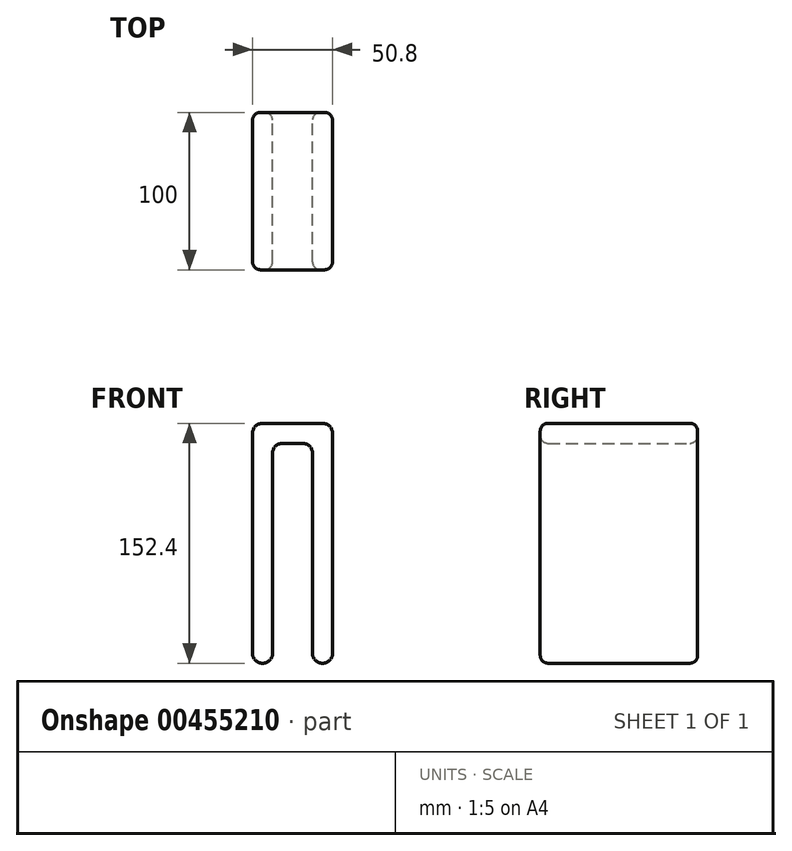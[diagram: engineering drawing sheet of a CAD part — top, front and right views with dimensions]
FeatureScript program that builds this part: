
annotation { "Feature Type Name" : "Feature", "Feature Type Description" : "" }
export const myFeature = defineFeature(function(context is Context, id is Id, definition is map)
    precondition{}
    {
        {
            var Q0;
            Q0=qCreatedBy(makeId("Front.planeOp"),FACE);
            var sketch = newSketch(context, id + "F0", { "sketchPlane" : qUnion([Q0])});
            skLineSegment(sketch, "E0.bottom", {"start": v(-19.05, 76.2) * mm, "end": v(19.05, 76.2) * mm});
            skLineSegment(sketch, "E0.top", {"start": v(-19.05, -76.2) * mm, "end": v(-19.05, -76.2) * mm});
            skLineSegment(sketch, "E0.left", {"start": v(-25.4, 69.85) * mm, "end": v(-25.4, -69.85) * mm});
            skLineSegment(sketch, "E0.right", {"start": v(25.4, 69.85) * mm, "end": v(25.4, -69.85) * mm});
            skPoint(sketch, "E0.middle", {"position": v(0, 0) * mm});
            skLineSegment(sketch, "E1.top", {"start": v(-6.35, 63.5) * mm, "end": v(6.35, 63.5) * mm});
            skLineSegment(sketch, "E1.left", {"start": v(-12.7, -63.5) * mm, "end": v(-12.7, 57.15) * mm});
            skLineSegment(sketch, "E1.right", {"start": v(12.7, -63.5) * mm, "end": v(12.7, 57.15) * mm});
            skLineSegment(sketch, "E2", {"start": v(-12.7, -63.5) * mm, "end": v(-12.7, -69.85) * mm});
            skLineSegment(sketch, "E3", {"start": v(12.7, -63.5) * mm, "end": v(12.7, -69.85) * mm});
            skLineSegment(sketch, "E4.trimOffspring", {"start": v(19.05, -76.2) * mm, "end": v(19.05, -76.2) * mm});
            skPoint(sketch, "E5.visualSharp", {"position": v(-12.7, 63.5) * mm});
            skArc(sketch, "E5.filletArc", {"start": v(-6.35, 63.5) * mm, "mid": v(-10.84, 61.64) * mm, "end": v(-12.7, 57.15) * mm});
            skPoint(sketch, "E6.visualSharp", {"position": v(-25.4, 76.2) * mm});
            skArc(sketch, "E6.filletArc", {"start": v(-19.05, 76.2) * mm, "mid": v(-23.54, 74.34) * mm, "end": v(-25.4, 69.85) * mm});
            skPoint(sketch, "E7.visualSharp", {"position": v(25.4, 76.2) * mm});
            skArc(sketch, "E7.filletArc", {"start": v(25.4, 69.85) * mm, "mid": v(23.54, 74.34) * mm, "end": v(19.05, 76.2) * mm});
            skPoint(sketch, "E8.visualSharp", {"position": v(12.7, 63.5) * mm});
            skArc(sketch, "E8.filletArc", {"start": v(12.7, 57.15) * mm, "mid": v(10.84, 61.64) * mm, "end": v(6.35, 63.5) * mm});
            skPoint(sketch, "E9.visualSharp", {"position": v(-25.4, -76.2) * mm});
            skArc(sketch, "E9.filletArc", {"start": v(-25.4, -69.85) * mm, "mid": v(-23.54, -74.34) * mm, "end": v(-19.05, -76.2) * mm});
            skPoint(sketch, "E10.visualSharp", {"position": v(12.7, -76.2) * mm});
            skArc(sketch, "E10.filletArc", {"start": v(12.7, -69.85) * mm, "mid": v(14.56, -74.34) * mm, "end": v(19.05, -76.2) * mm});
            skPoint(sketch, "E11.visualSharp", {"position": v(-12.7, -76.2) * mm});
            skArc(sketch, "E11.filletArc", {"start": v(-19.05, -76.2) * mm, "mid": v(-14.56, -74.34) * mm, "end": v(-12.7, -69.85) * mm});
            skPoint(sketch, "E12.visualSharp", {"position": v(25.4, -76.2) * mm});
            skArc(sketch, "E12.filletArc", {"start": v(19.05, -76.2) * mm, "mid": v(23.54, -74.34) * mm, "end": v(25.4, -69.85) * mm});
            skSolve(sketch);
        }
        {
            var Q0;
            Q0 = qSketchRegion(id + "F0", true);
            extrude(context, id + "F1", {"entities" : qUnion([Q0]), "endBound" : BoundingType.SYMMETRIC, "depth" : 100 * mm});
        }
        {
            var Q0;
            Q0=makeQuery(id+"F1.opExtrude","CAP_FACE",FACE,{"disambiguationData":[OSD([sQuery(id+"F0.wireOp",EDGE,"E0.bottom"),sQuery(id+"F0.wireOp",EDGE,"E0.left"),sQuery(id+"F0.wireOp",EDGE,"E0.right"),sQuery(id+"F0.wireOp",EDGE,"E1.top"),sQuery(id+"F0.wireOp",EDGE,"E1.left"),sQuery(id+"F0.wireOp",EDGE,"E1.right"),sQuery(id+"F0.wireOp",EDGE,"E2"),sQuery(id+"F0.wireOp",EDGE,"E3"),sQuery(id+"F0.wireOp",EDGE,"E5.filletArc"),sQuery(id+"F0.wireOp",EDGE,"E6.filletArc"),sQuery(id+"F0.wireOp",EDGE,"E7.filletArc"),sQuery(id+"F0.wireOp",EDGE,"E8.filletArc"),sQuery(id+"F0.wireOp",EDGE,"E9.filletArc"),sQuery(id+"F0.wireOp",EDGE,"E10.filletArc"),sQuery(id+"F0.wireOp",EDGE,"E11.filletArc"),sQuery(id+"F0.wireOp",EDGE,"E12.filletArc")])],"isStart":true});
            var Q1;
            Q1=makeQuery(id+"F1.opExtrude","CAP_EDGE",EDGE,{"disambiguationData":[OSD([sQuery(id+"F0.wireOp",EDGE,"E10.filletArc"),sQuery(id+"F0.wireOp",EDGE,"E12.filletArc")])],"isStart":false});
            fillet(context, id + "F2", {"entities" : qUnion([Q0, Q1]), "radius" : 5 * mm, "tangentPropagation" : true, "allowEdgeOverflow" : false});
        }
    });
